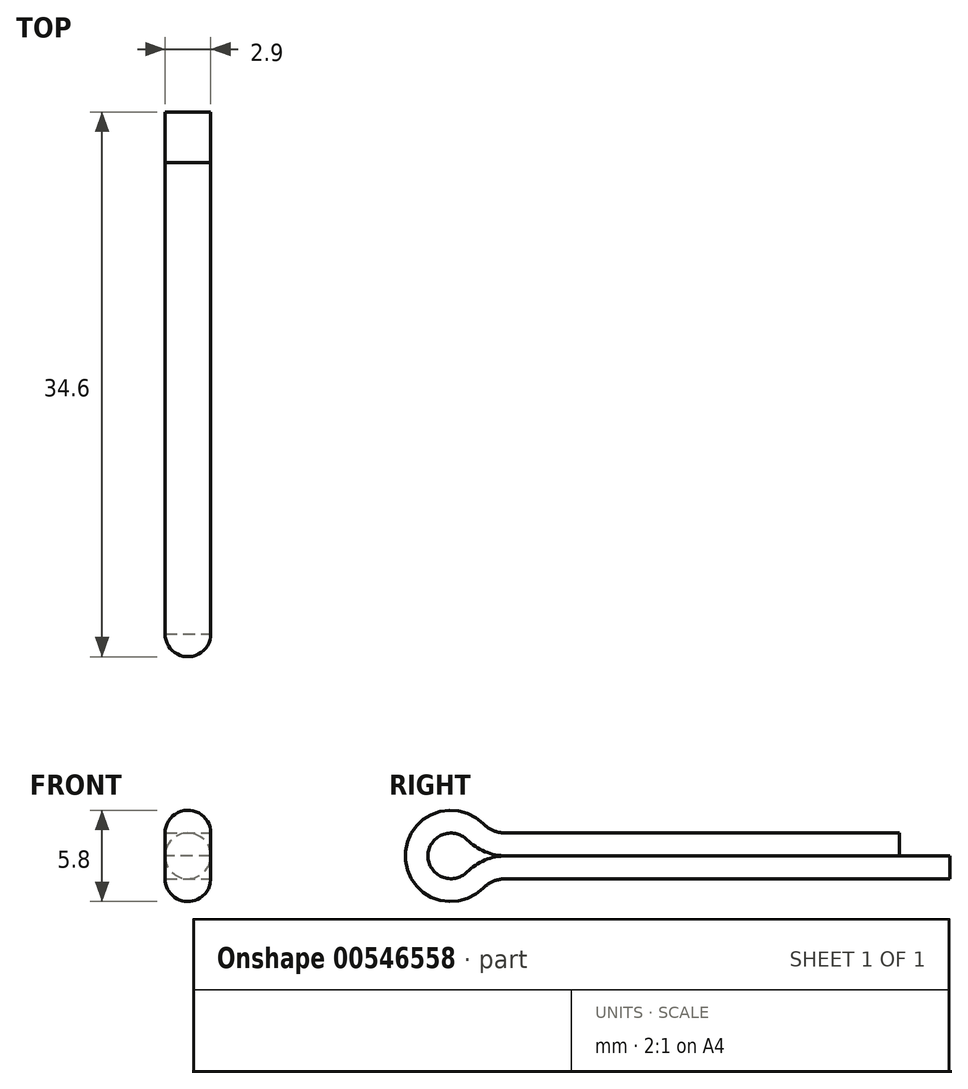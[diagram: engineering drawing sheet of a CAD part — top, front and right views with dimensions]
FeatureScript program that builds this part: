
annotation { "Feature Type Name" : "Feature", "Feature Type Description" : "" }
export const myFeature = defineFeature(function(context is Context, id is Id, definition is map)
    precondition{}
    {
        {
            var Q0;
            Q0=qCreatedBy(makeId("Right.planeOp"),FACE);
            var sketch = newSketch(context, id + "F0", { "sketchPlane" : qUnion([Q0])});
            skLineSegment(sketch, "E0", {"start": v(0, 1.45) * mm, "end": v(25, 1.45) * mm});
            skArc(sketch, "E1", {"start": v(0, 1.45) * mm, "mid": v(-0.78, 1.6) * mm, "end": v(-1.45, 2.05) * mm});
            skLineSegment(sketch, "E2", {"start": v(0, 0) * mm, "end": v(28.87, 0) * mm, "construction": true});
            skLineSegment(sketch, "E3.MirrorCS", {"start": v(0, -1.45) * mm, "end": v(28.2, -1.45) * mm});
            skArc(sketch, "E4.MirrorCS", {"start": v(0, -1.45) * mm, "mid": v(-0.78, -1.6) * mm, "end": v(-1.45, -2.05) * mm});
            skArc(sketch, "E5", {"start": v(-1.45, 2.05) * mm, "mid": v(-6.4, 0) * mm, "end": v(-1.45, -2.05) * mm});
            skSolve(sketch);
        }
        {
            var Q0;
            Q0=qCreatedBy(makeId("Front.planeOp"),FACE);
            var Q1;
            Q1=sQuery(id+"F0.wireOp",VERTEX,"E0.end");
            cPlane(context, id + "F1", {"entities" : qUnion([Q0, Q1]), "cplaneType" : CPlaneType.PLANE_POINT, "offset" : 25 * mm, "width" : 150 * mm, "height" : 150 * mm});
        }
        {
            var Q0;
            Q0=qCreatedBy(id+"F1.planeOp",FACE);
            var sketch = newSketch(context, id + "F2", { "sketchPlane" : qUnion([Q0])});
            skArc(sketch, "E6", {"start": v(1.45, 0) * mm, "mid": v(0, 1.45) * mm, "end": v(-1.45, 0) * mm});
            skLineSegment(sketch, "E7", {"start": v(1.7, 0) * mm, "end": v(-1.86, 0) * mm, "construction": true});
            skLineSegment(sketch, "E8", {"start": v(1.45, 0) * mm, "end": v(-1.45, 0) * mm});
            skSolve(sketch);
        }
        {
            var Q0;
            Q0=makeQuery(id+"F2.imprint","IMPRINT",FACE,{"disambiguationData":[TD([[makeQuery(id+"F2.imprint","IMPRINT",EDGE,{"derivedFrom":sQuery(id+"F2.wireOp",EDGE,"E6")}),1.0]])]});
            var Q1;
            Q1=sQuery(id+"F0.wireOp",EDGE,"E0");
            var Q2;
            Q2=sQuery(id+"F0.wireOp",EDGE,"E1");
            var Q3;
            Q3=sQuery(id+"F0.wireOp",EDGE,"E5");
            var Q4;
            Q4=sQuery(id+"F0.wireOp",EDGE,"E4.MirrorCS");
            var Q5;
            Q5=sQuery(id+"F0.wireOp",EDGE,"E3.MirrorCS");
            sweep(context, id + "F3", {"profiles" : qUnion([Q0]), "path" : qUnion([Q1, Q2, Q3, Q4, Q5])});
        }
    });
